# Revit family: PlainRecessedLightingFixtureMod
name_source: partatom
category: Lighting Fixtures
revit_build: Autodesk Revit MEP 2012 (Build: 20110916_2132(x64)
units: mm (PartAtom-declared; Revit-internal decimal feet)

## types (8) — shared parameters
Color Filter = 16777215
Default Elevation = 4' - 0"
Depth = 0' - 6"
Dimming Lamp Color Temperature Shift = <None>
Emit Shape Visible in Rendering = No
Load Classification = Lighting - Dwelling Unit
Tilt Angle = -90.00°

## per-type parameters (varying)
| type | Apparent Load | Ballast Voltage | Emit from Rectangle Length | Emit from Rectangle Width | Length | Photometric Web File | Width |
| 1x4 - 120 | 64 VA | 120 V | 4' - 0" | 1' - 0" | 4' - 0" | 1x42A12.ies | 1' - 0" |
| 1x4 - 277 | 64 VA | 277 V | 4' - 0" | 1' - 0" | 4' - 0" | 1x42A12.ies | 1' - 0" |
| 20x4 - 120 | 64 VA | 120 V | 4' - 0" | 1' - 8" | 4' - 0" | 20x42A12.ies | 1' - 8" |
| 20x4 - 277 | 64 VA | 277 V | 4' - 0" | 1' - 8" | 4' - 0" | 20x42A12.ies | 1' - 8" |
| 2x2 - 120 | 62 VA | 120 V | 2' - 0" | 2' - 0" | 2' - 0" | 2x22UA12.ies | 2' - 0" |
| 2x2 - 277 | 62 VA | 277 V | 2' - 0" | 2' - 0" | 2' - 0" | 2x22UA12.ies | 2' - 0" |
| 2x4 - 120 | 96 VA | 120 V | 4' - 0" | 2' - 0" | 4' - 0" | 2x43A12.ies | 2' - 0" |
| 2x4 - 277 | 96 VA | 277 V | 4' - 0" | 2' - 0" | 4' - 0" | 2x43A12.ies | 2' - 0" |

## geometry (parser evidence)
native form markers: Sweep x3
no freeform markers — native parametric forms only
